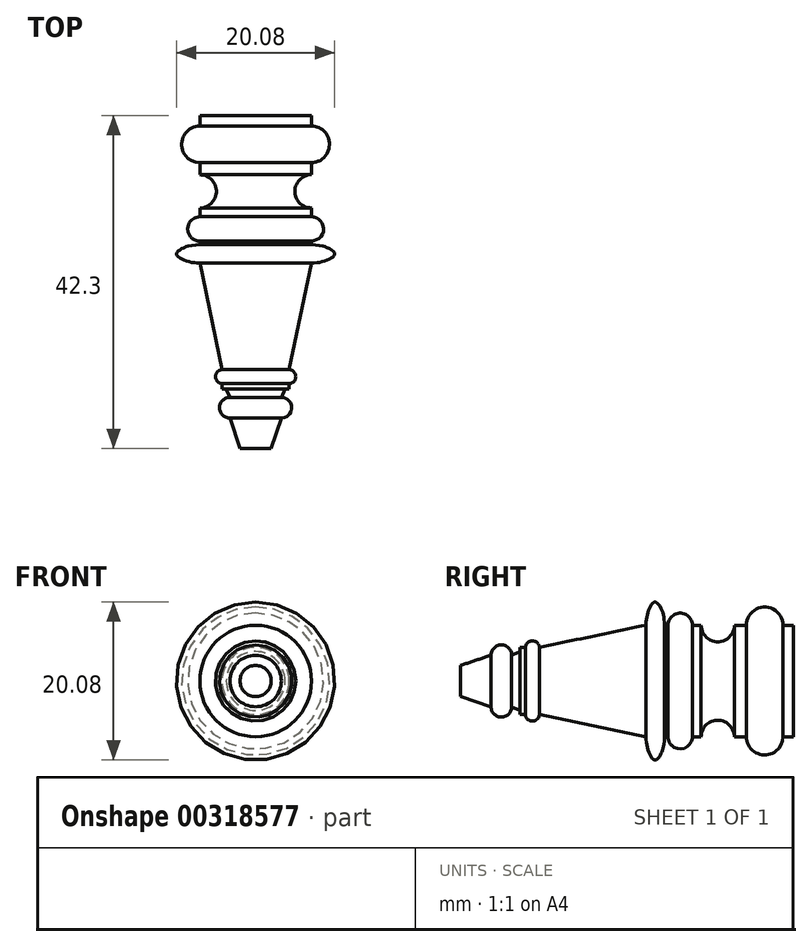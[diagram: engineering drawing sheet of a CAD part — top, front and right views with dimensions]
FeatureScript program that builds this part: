
annotation { "Feature Type Name" : "Feature", "Feature Type Description" : "" }
export const myFeature = defineFeature(function(context is Context, id is Id, definition is map)
    precondition{}
    {
        {
            var Q0;
            Q0=qCreatedBy(makeId("Top.planeOp"),FACE);
            var sketch = newSketch(context, id + "F0", { "sketchPlane" : qUnion([Q0])});
            skLineSegment(sketch, "E0", {"start": v(-7.09, 45.44) * mm, "end": v(-7.09, 44.08) * mm});
            skArc(sketch, "E1", {"start": v(-7.09, 44.08) * mm, "mid": v(-9.4, 41.77) * mm, "end": v(-7.09, 39.45) * mm});
            skLineSegment(sketch, "E2", {"start": v(-7.09, 39.45) * mm, "end": v(-7.09, 37.9) * mm});
            skArc(sketch, "E3", {"start": v(-7.09, 33.7) * mm, "mid": v(-4.98, 35.8) * mm, "end": v(-7.09, 37.9) * mm});
            skLineSegment(sketch, "E4", {"start": v(-7.09, 33.7) * mm, "end": v(-7.09, 32.58) * mm});
            skArc(sketch, "E5", {"start": v(-7.09, 32.58) * mm, "mid": v(-8.63, 31.03) * mm, "end": v(-7.09, 29.5) * mm});
            skLineSegment(sketch, "E6", {"start": v(-7.09, 29.5) * mm, "end": v(-7.09, 29.03) * mm});
            skFitSpline(sketch, "E7", {"points": [v(-7.09, 29.03) * mm, v(-9.09, 28.66) * mm, v(-10.04, 27.82) * mm, v(-9.06, 27.06) * mm, v(-7.09, 26.67) * mm], "startDerivative": vector(-9.09, -0.32) * mm, "endDerivative": vector(9.74, -0.6) * mm});
            skLineSegment(sketch, "E8", {"start": v(-7.09, 26.67) * mm, "end": v(-4.27, 13.15) * mm});
            skArc(sketch, "E9", {"start": v(-4.27, 13.15) * mm, "mid": v(-5.1, 12.26) * mm, "end": v(-4.27, 11.38) * mm});
            skLineSegment(sketch, "E10", {"start": v(-4.27, 11.38) * mm, "end": v(-4.27, 10.67) * mm});
            skLineSegment(sketch, "E11", {"start": v(-3.74, 10.67) * mm, "end": v(-3.27, 9.63) * mm});
            skArc(sketch, "E12", {"start": v(-3.27, 9.63) * mm, "mid": v(-4.59, 8.31) * mm, "end": v(-3.27, 7) * mm});
            skLineSegment(sketch, "E13", {"start": v(-3.27, 7) * mm, "end": v(-1.98, 3.14) * mm});
            skLineSegment(sketch, "E14", {"start": v(-4.27, 10.67) * mm, "end": v(-3.74, 10.67) * mm});
            skLineSegment(sketch, "E15", {"start": v(0, 45.44) * mm, "end": v(0, 3.14) * mm, "construction": true});
            skLineSegment(sketch, "E16", {"start": v(-1.98, 3.14) * mm, "end": v(0, 3.14) * mm});
            skLineSegment(sketch, "E17", {"start": v(-7.09, 45.44) * mm, "end": v(0, 45.44) * mm});
            skLineSegment(sketch, "E18", {"start": v(0, 45.44) * mm, "end": v(0, 3.14) * mm});
            skSolve(sketch);
        }
        {
            var Q0;
            Q0=makeQuery(id+"F0.imprint","IMPRINT",FACE,{"disambiguationData":[TD([[makeQuery(id+"F0.imprint","IMPRINT",EDGE,{"derivedFrom":sQuery(id+"F0.wireOp",EDGE,"E0")}),1.0]])]});
            var Q1;
            Q1=sQuery(id+"F0.wireOp",EDGE,"E18");
            revolve(context, id + "F1", {"entities" : qUnion([Q0]), "axis" : qUnion([Q1]), "revolveType" : RevolveType.FULL});
        }
    });
